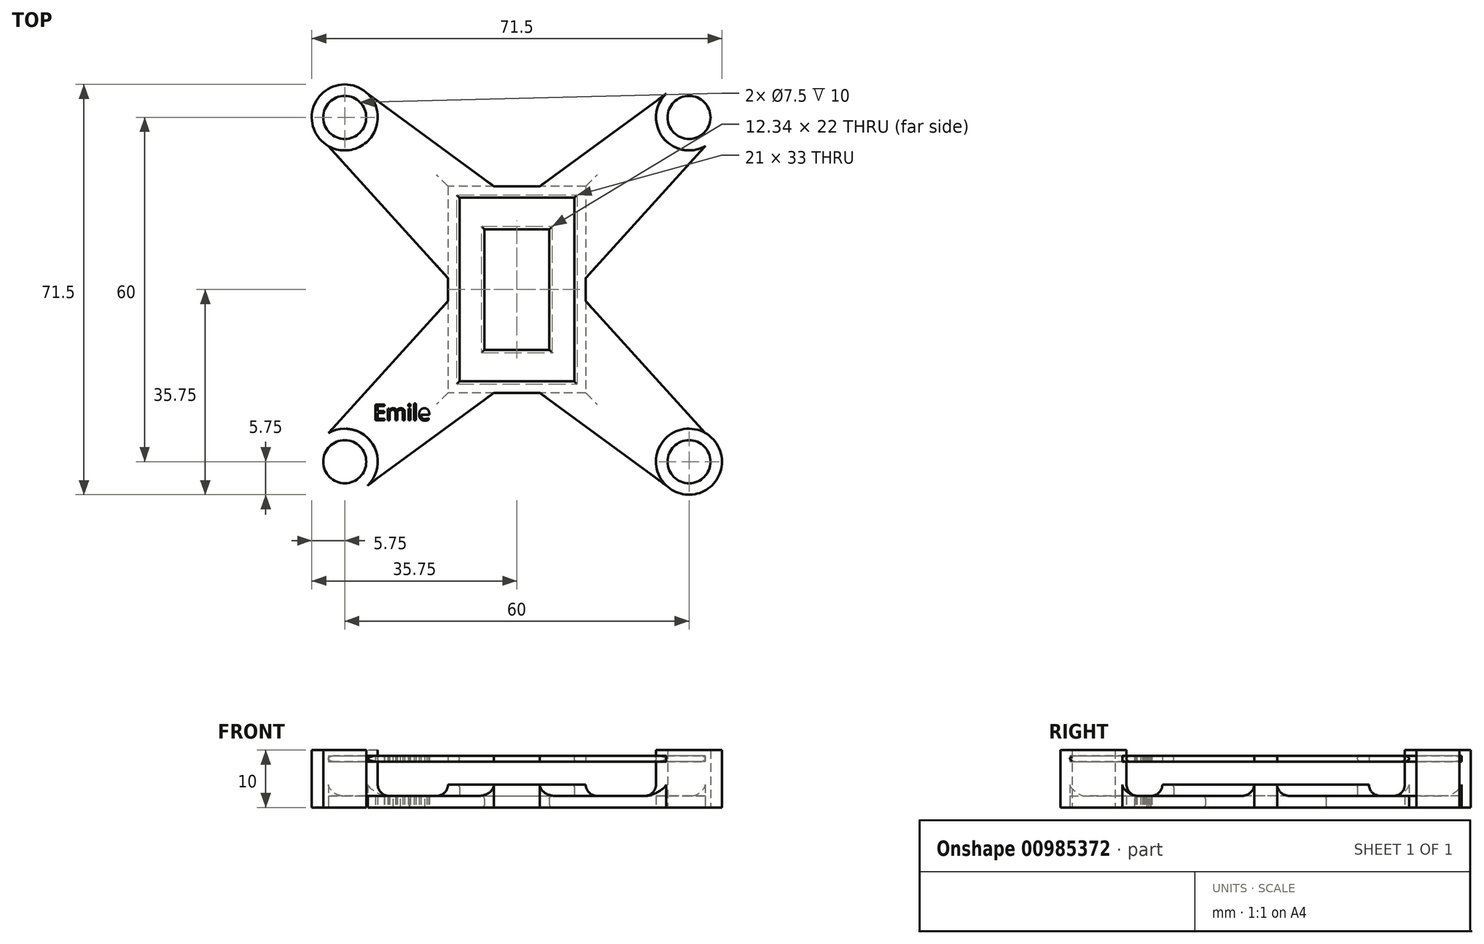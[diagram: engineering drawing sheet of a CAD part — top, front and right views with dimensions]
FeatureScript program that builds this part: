
annotation { "Feature Type Name" : "Feature", "Feature Type Description" : "" }
export const myFeature = defineFeature(function(context is Context, id is Id, definition is map)
    precondition{}
    {
        {
            var Q0;
            Q0=qCreatedBy(makeId("Top.planeOp"),FACE);
            var sketch = newSketch(context, id + "F0", { "sketchPlane" : qUnion([Q0])});
            skLineSegment(sketch, "E0.bottom", {"start": v(30, -30) * mm, "end": v(-30, -30) * mm, "construction": true});
            skLineSegment(sketch, "E0.top", {"start": v(30, 30) * mm, "end": v(-30, 30) * mm, "construction": true});
            skLineSegment(sketch, "E0.left", {"start": v(30, -30) * mm, "end": v(30, 30) * mm, "construction": true});
            skLineSegment(sketch, "E0.right", {"start": v(-30, -30) * mm, "end": v(-30, 30) * mm, "construction": true});
            skPoint(sketch, "E0.middle", {"position": v(0, 0) * mm});
            skCircle(sketch, "E1", {"center": v(-30, 30) * mm, "radius": 3.75 * mm});
            skCircle(sketch, "E2.MirrorC", {"center": v(30, 30) * mm, "radius": 3.75 * mm});
            skCircle(sketch, "E3.MirrorC", {"center": v(-30, -30) * mm, "radius": 3.75 * mm});
            skCircle(sketch, "E4.MirrorC", {"center": v(30, -30) * mm, "radius": 3.75 * mm});
            skCircle(sketch, "E5", {"center": v(-30, 30) * mm, "radius": 5.75 * mm});
            skCircle(sketch, "E6.MirrorC", {"center": v(30, 30) * mm, "radius": 5.75 * mm});
            skCircle(sketch, "E7.MirrorC", {"center": v(30, -30) * mm, "radius": 5.75 * mm});
            skCircle(sketch, "E8.MirrorC", {"center": v(-30, -30) * mm, "radius": 5.75 * mm});
            skLineSegment(sketch, "E9.bottom", {"start": v(10, -16) * mm, "end": v(-10, -16) * mm});
            skLineSegment(sketch, "E9.top", {"start": v(10, 16) * mm, "end": v(-10, 16) * mm});
            skLineSegment(sketch, "E9.left", {"start": v(10, -16) * mm, "end": v(10, 16) * mm});
            skLineSegment(sketch, "E9.right", {"start": v(-10, -16) * mm, "end": v(-10, 16) * mm});
            skLineSegment(sketch, "E10.bottom", {"start": v(12, 18) * mm, "end": v(-12, 18) * mm});
            skLineSegment(sketch, "E10.top", {"start": v(12, -18) * mm, "end": v(-12, -18) * mm});
            skLineSegment(sketch, "E10.left", {"start": v(12, 18) * mm, "end": v(12, -18) * mm});
            skLineSegment(sketch, "E10.right", {"start": v(-12, 18) * mm, "end": v(-12, -18) * mm});
            skLineSegment(sketch, "E11", {"start": v(-26, 34.13) * mm, "end": v(-4, 18) * mm});
            skLineSegment(sketch, "E12", {"start": v(-32.84, 25) * mm, "end": v(-12, 2) * mm});
            skLineSegment(sketch, "E13.MirrorCS", {"start": v(26, 34.13) * mm, "end": v(4, 18) * mm});
            skLineSegment(sketch, "E14.MirrorCS", {"start": v(32.84, 25) * mm, "end": v(12, 2) * mm});
            skLineSegment(sketch, "E15.MirrorCS", {"start": v(-32.84, -25) * mm, "end": v(-12, -2) * mm});
            skLineSegment(sketch, "E16.MirrorCS", {"start": v(-26, -34.13) * mm, "end": v(-4, -18) * mm});
            skLineSegment(sketch, "E17.MirrorCS", {"start": v(26, -34.13) * mm, "end": v(4, -18) * mm});
            skLineSegment(sketch, "E18.MirrorCS", {"start": v(32.84, -25) * mm, "end": v(12, -2) * mm});
            skLineSegment(sketch, "E19.bottom", {"start": v(-5.67, 10.5) * mm, "end": v(5.67, 10.5) * mm});
            skLineSegment(sketch, "E19.top", {"start": v(-5.67, -10.5) * mm, "end": v(5.67, -10.5) * mm});
            skLineSegment(sketch, "E19.left", {"start": v(-5.67, 10.5) * mm, "end": v(-5.67, -10.5) * mm});
            skLineSegment(sketch, "E19.right", {"start": v(5.67, 10.5) * mm, "end": v(5.67, -10.5) * mm});
            skText(sketch, "E20", { "text": "Emile\n", "fontName": "OpenSans-Regular.ttf"});
            const initialGuessF0  = {"E20": [-0.025, -0.0228, 1, 0, 0.0028]};
            skSetInitialGuess(sketch, initialGuessF0);
            skSolve(sketch);
        }
        {
            var Q0;
            Q0=makeQuery(id+"F0.imprint","IMPRINT",FACE,{"disambiguationData":[TD([[makeQuery(id+"F0.imprint","IMPRINT",EDGE,{"derivedFrom":sQuery(id+"F0.wireOp",EDGE,"E9.bottom")}),1.0]])]});
            var Q1;
            Q1=makeQuery(id+"F0.imprint","IMPRINT",FACE,{"disambiguationData":[TD([[makeQuery(id+"F0.imprint","IMPRINT",EDGE,{"derivedFrom":sQuery(id+"F0.wireOp",EDGE,"E9.bottom")}),-1.0]])]});
            var Q2;
            {var subQ0=sQuery(id+"F0.wireOp",EDGE,"E11");Q2=makeQuery(id+"F0.imprint","IMPRINT",FACE,{"disambiguationData":[TD([[makeQuery(id+"F0.imprint","IMPRINT",EDGE,{"derivedFrom":subQ0}),-1.0]])]});}
            var Q3;
            {var subQ0=sQuery(id+"F0.wireOp",EDGE,"E15.MirrorCS");Q3=makeQuery(id+"F0.imprint","IMPRINT",FACE,{"disambiguationData":[TD([[makeQuery(id+"F0.imprint","IMPRINT",EDGE,{"derivedFrom":subQ0}),-1.0]])]});}
            var Q4;
            {var subQ0=sQuery(id+"F0.wireOp",EDGE,"E17.MirrorCS");Q4=makeQuery(id+"F0.imprint","IMPRINT",FACE,{"disambiguationData":[TD([[makeQuery(id+"F0.imprint","IMPRINT",EDGE,{"derivedFrom":subQ0}),-1.0]])]});}
            var Q5;
            {var subQ0=sQuery(id+"F0.wireOp",EDGE,"E13.MirrorCS");Q5=makeQuery(id+"F0.imprint","IMPRINT",FACE,{"disambiguationData":[TD([[makeQuery(id+"F0.imprint","IMPRINT",EDGE,{"derivedFrom":subQ0}),1.0]])]});}
            var Q6;
            Q6=makeQuery(id+"F0.imprint","IMPRINT",FACE,{"disambiguationData":[TD([[makeQuery(id+"F0.imprint","IMPRINT",EDGE,{"derivedFrom":sQuery(id+"F0.wireOp",EDGE,"E1")}),-1.0]])]});
            var Q7;
            Q7=makeQuery(id+"F0.imprint","IMPRINT",FACE,{"disambiguationData":[TD([[makeQuery(id+"F0.imprint","IMPRINT",EDGE,{"derivedFrom":sQuery(id+"F0.wireOp",EDGE,"E2.MirrorC")}),1.0]])]});
            var Q8;
            Q8=makeQuery(id+"F0.imprint","IMPRINT",FACE,{"disambiguationData":[TD([[makeQuery(id+"F0.imprint","IMPRINT",EDGE,{"derivedFrom":sQuery(id+"F0.wireOp",EDGE,"E4.MirrorC")}),-1.0]])]});
            var Q9;
            Q9=makeQuery(id+"F0.imprint","IMPRINT",FACE,{"disambiguationData":[TD([[makeQuery(id+"F0.imprint","IMPRINT",EDGE,{"derivedFrom":sQuery(id+"F0.wireOp",EDGE,"E3.MirrorC")}),1.0]])]});
            extrude(context, id + "F1", {"entities" : qUnion([Q0, Q1, Q2, Q3, Q4, Q5, Q6, Q7, Q8, Q9]), "depth" : 2 * mm, "offsetDistance" : 25 * mm});
        }
        {
            var Q0;
            Q0=makeQuery(id+"F0.imprint","IMPRINT",FACE,{"disambiguationData":[TD([[makeQuery(id+"F0.imprint","IMPRINT",EDGE,{"derivedFrom":sQuery(id+"F0.wireOp",EDGE,"E1")}),-1.0]])]});
            var Q1;
            Q1=makeQuery(id+"F0.imprint","IMPRINT",FACE,{"disambiguationData":[TD([[makeQuery(id+"F0.imprint","IMPRINT",EDGE,{"derivedFrom":sQuery(id+"F0.wireOp",EDGE,"E2.MirrorC")}),1.0]])]});
            var Q2;
            Q2=makeQuery(id+"F0.imprint","IMPRINT",FACE,{"disambiguationData":[TD([[makeQuery(id+"F0.imprint","IMPRINT",EDGE,{"derivedFrom":sQuery(id+"F0.wireOp",EDGE,"E4.MirrorC")}),-1.0]])]});
            var Q3;
            Q3=makeQuery(id+"F0.imprint","IMPRINT",FACE,{"disambiguationData":[TD([[makeQuery(id+"F0.imprint","IMPRINT",EDGE,{"derivedFrom":sQuery(id+"F0.wireOp",EDGE,"E3.MirrorC")}),1.0]])]});
            extrude(context, id + "F2", {"entities" : qUnion([Q0, Q1, Q2, Q3]), "operationType" : NewBodyOperationType.ADD, "depth" : 10 * mm, "offsetDistance" : 25 * mm});
        }
        {
            var Q0;
            Q0=makeQuery(id+"F0.imprint","IMPRINT",FACE,{"disambiguationData":[TD([[makeQuery(id+"F0.imprint","IMPRINT",EDGE,{"derivedFrom":sQuery(id+"F0.wireOp",EDGE,"E9.bottom")}),1.0]])]});
            extrude(context, id + "F3", {"entities" : qUnion([Q0]), "operationType" : NewBodyOperationType.ADD, "depth" : 4 * mm, "offsetDistance" : 25 * mm});
        }
        {
            var Q0;
            {var subQ0=sQuery(id+"F0.wireOp",EDGE,"E5");Q0=makeQuery(id+"F2.boolean.opBoolean","INTERSECT",EDGE,{"derivedFrom":[makeQuery(id+"F1.opExtrude","CAP_FACE",FACE,{"disambiguationData":[OSD([sQuery(id+"F0.wireOp",EDGE,"E1"),sQuery(id+"F0.wireOp",EDGE,"E2.MirrorC"),sQuery(id+"F0.wireOp",EDGE,"E3.MirrorC"),sQuery(id+"F0.wireOp",EDGE,"E4.MirrorC"),subQ0,sQuery(id+"F0.wireOp",EDGE,"E6.MirrorC"),sQuery(id+"F0.wireOp",EDGE,"E7.MirrorC"),sQuery(id+"F0.wireOp",EDGE,"E8.MirrorC"),sQuery(id+"F0.wireOp",EDGE,"E10.bottom"),sQuery(id+"F0.wireOp",EDGE,"E10.top"),sQuery(id+"F0.wireOp",EDGE,"E10.left"),sQuery(id+"F0.wireOp",EDGE,"E10.right"),sQuery(id+"F0.wireOp",EDGE,"E11"),sQuery(id+"F0.wireOp",EDGE,"E12"),sQuery(id+"F0.wireOp",EDGE,"E13.MirrorCS"),sQuery(id+"F0.wireOp",EDGE,"E14.MirrorCS"),sQuery(id+"F0.wireOp",EDGE,"E15.MirrorCS"),sQuery(id+"F0.wireOp",EDGE,"E16.MirrorCS"),sQuery(id+"F0.wireOp",EDGE,"E17.MirrorCS"),sQuery(id+"F0.wireOp",EDGE,"E18.MirrorCS"),sQuery(id+"F0.wireOp",EDGE,"E19.bottom"),sQuery(id+"F0.wireOp",EDGE,"E19.top"),sQuery(id+"F0.wireOp",EDGE,"E19.left"),sQuery(id+"F0.wireOp",EDGE,"E19.right")])],"isStart":false}),makeQuery(id+"F2.opExtrude","SWEPT_FACE",FACE,{"disambiguationData":[OSD([subQ0])]})]});}
            var Q1;
            {var subQ0=sQuery(id+"F0.wireOp",EDGE,"E6.MirrorC");Q1=makeQuery(id+"F2.boolean.opBoolean","INTERSECT",EDGE,{"derivedFrom":[makeQuery(id+"F1.opExtrude","CAP_FACE",FACE,{"disambiguationData":[OSD([sQuery(id+"F0.wireOp",EDGE,"E1"),sQuery(id+"F0.wireOp",EDGE,"E2.MirrorC"),sQuery(id+"F0.wireOp",EDGE,"E3.MirrorC"),sQuery(id+"F0.wireOp",EDGE,"E4.MirrorC"),sQuery(id+"F0.wireOp",EDGE,"E5"),subQ0,sQuery(id+"F0.wireOp",EDGE,"E7.MirrorC"),sQuery(id+"F0.wireOp",EDGE,"E8.MirrorC"),sQuery(id+"F0.wireOp",EDGE,"E10.bottom"),sQuery(id+"F0.wireOp",EDGE,"E10.top"),sQuery(id+"F0.wireOp",EDGE,"E10.left"),sQuery(id+"F0.wireOp",EDGE,"E10.right"),sQuery(id+"F0.wireOp",EDGE,"E11"),sQuery(id+"F0.wireOp",EDGE,"E12"),sQuery(id+"F0.wireOp",EDGE,"E13.MirrorCS"),sQuery(id+"F0.wireOp",EDGE,"E14.MirrorCS"),sQuery(id+"F0.wireOp",EDGE,"E15.MirrorCS"),sQuery(id+"F0.wireOp",EDGE,"E16.MirrorCS"),sQuery(id+"F0.wireOp",EDGE,"E17.MirrorCS"),sQuery(id+"F0.wireOp",EDGE,"E18.MirrorCS"),sQuery(id+"F0.wireOp",EDGE,"E19.bottom"),sQuery(id+"F0.wireOp",EDGE,"E19.top"),sQuery(id+"F0.wireOp",EDGE,"E19.left"),sQuery(id+"F0.wireOp",EDGE,"E19.right")])],"isStart":false}),makeQuery(id+"F2.opExtrude","SWEPT_FACE",FACE,{"disambiguationData":[OSD([subQ0])]})]});}
            var Q2;
            {var subQ0=sQuery(id+"F0.wireOp",EDGE,"E7.MirrorC");Q2=makeQuery(id+"F2.boolean.opBoolean","INTERSECT",EDGE,{"derivedFrom":[makeQuery(id+"F1.opExtrude","CAP_FACE",FACE,{"disambiguationData":[OSD([sQuery(id+"F0.wireOp",EDGE,"E1"),sQuery(id+"F0.wireOp",EDGE,"E2.MirrorC"),sQuery(id+"F0.wireOp",EDGE,"E3.MirrorC"),sQuery(id+"F0.wireOp",EDGE,"E4.MirrorC"),sQuery(id+"F0.wireOp",EDGE,"E5"),sQuery(id+"F0.wireOp",EDGE,"E6.MirrorC"),subQ0,sQuery(id+"F0.wireOp",EDGE,"E8.MirrorC"),sQuery(id+"F0.wireOp",EDGE,"E10.bottom"),sQuery(id+"F0.wireOp",EDGE,"E10.top"),sQuery(id+"F0.wireOp",EDGE,"E10.left"),sQuery(id+"F0.wireOp",EDGE,"E10.right"),sQuery(id+"F0.wireOp",EDGE,"E11"),sQuery(id+"F0.wireOp",EDGE,"E12"),sQuery(id+"F0.wireOp",EDGE,"E13.MirrorCS"),sQuery(id+"F0.wireOp",EDGE,"E14.MirrorCS"),sQuery(id+"F0.wireOp",EDGE,"E15.MirrorCS"),sQuery(id+"F0.wireOp",EDGE,"E16.MirrorCS"),sQuery(id+"F0.wireOp",EDGE,"E17.MirrorCS"),sQuery(id+"F0.wireOp",EDGE,"E18.MirrorCS"),sQuery(id+"F0.wireOp",EDGE,"E19.bottom"),sQuery(id+"F0.wireOp",EDGE,"E19.top"),sQuery(id+"F0.wireOp",EDGE,"E19.left"),sQuery(id+"F0.wireOp",EDGE,"E19.right")])],"isStart":false}),makeQuery(id+"F2.opExtrude","SWEPT_FACE",FACE,{"disambiguationData":[OSD([subQ0])]})]});}
            var Q3;
            {var subQ0=sQuery(id+"F0.wireOp",EDGE,"E8.MirrorC");Q3=makeQuery(id+"F2.boolean.opBoolean","INTERSECT",EDGE,{"derivedFrom":[makeQuery(id+"F1.opExtrude","CAP_FACE",FACE,{"disambiguationData":[OSD([sQuery(id+"F0.wireOp",EDGE,"E1"),sQuery(id+"F0.wireOp",EDGE,"E2.MirrorC"),sQuery(id+"F0.wireOp",EDGE,"E3.MirrorC"),sQuery(id+"F0.wireOp",EDGE,"E4.MirrorC"),sQuery(id+"F0.wireOp",EDGE,"E5"),sQuery(id+"F0.wireOp",EDGE,"E6.MirrorC"),sQuery(id+"F0.wireOp",EDGE,"E7.MirrorC"),subQ0,sQuery(id+"F0.wireOp",EDGE,"E10.bottom"),sQuery(id+"F0.wireOp",EDGE,"E10.top"),sQuery(id+"F0.wireOp",EDGE,"E10.left"),sQuery(id+"F0.wireOp",EDGE,"E10.right"),sQuery(id+"F0.wireOp",EDGE,"E11"),sQuery(id+"F0.wireOp",EDGE,"E12"),sQuery(id+"F0.wireOp",EDGE,"E13.MirrorCS"),sQuery(id+"F0.wireOp",EDGE,"E14.MirrorCS"),sQuery(id+"F0.wireOp",EDGE,"E15.MirrorCS"),sQuery(id+"F0.wireOp",EDGE,"E16.MirrorCS"),sQuery(id+"F0.wireOp",EDGE,"E17.MirrorCS"),sQuery(id+"F0.wireOp",EDGE,"E18.MirrorCS"),sQuery(id+"F0.wireOp",EDGE,"E19.bottom"),sQuery(id+"F0.wireOp",EDGE,"E19.top"),sQuery(id+"F0.wireOp",EDGE,"E19.left"),sQuery(id+"F0.wireOp",EDGE,"E19.right")])],"isStart":false}),makeQuery(id+"F2.opExtrude","SWEPT_FACE",FACE,{"disambiguationData":[OSD([subQ0])]})]});}
            var Q4;
            {var subQ0=sQuery(id+"F0.wireOp",EDGE,"E10.right");Q4=makeQuery(id+"F3.boolean.opBoolean","INTERSECT",EDGE,{"disambiguationData":[OD(1.0)],"derivedFrom":[makeQuery(id+"F1.opExtrude","CAP_FACE",FACE,{"disambiguationData":[OSD([sQuery(id+"F0.wireOp",EDGE,"E1"),sQuery(id+"F0.wireOp",EDGE,"E2.MirrorC"),sQuery(id+"F0.wireOp",EDGE,"E3.MirrorC"),sQuery(id+"F0.wireOp",EDGE,"E4.MirrorC"),sQuery(id+"F0.wireOp",EDGE,"E5"),sQuery(id+"F0.wireOp",EDGE,"E6.MirrorC"),sQuery(id+"F0.wireOp",EDGE,"E7.MirrorC"),sQuery(id+"F0.wireOp",EDGE,"E8.MirrorC"),sQuery(id+"F0.wireOp",EDGE,"E10.bottom"),sQuery(id+"F0.wireOp",EDGE,"E10.top"),sQuery(id+"F0.wireOp",EDGE,"E10.left"),subQ0,sQuery(id+"F0.wireOp",EDGE,"E11"),sQuery(id+"F0.wireOp",EDGE,"E12"),sQuery(id+"F0.wireOp",EDGE,"E13.MirrorCS"),sQuery(id+"F0.wireOp",EDGE,"E14.MirrorCS"),sQuery(id+"F0.wireOp",EDGE,"E15.MirrorCS"),sQuery(id+"F0.wireOp",EDGE,"E16.MirrorCS"),sQuery(id+"F0.wireOp",EDGE,"E17.MirrorCS"),sQuery(id+"F0.wireOp",EDGE,"E18.MirrorCS"),sQuery(id+"F0.wireOp",EDGE,"E19.bottom"),sQuery(id+"F0.wireOp",EDGE,"E19.top"),sQuery(id+"F0.wireOp",EDGE,"E19.left"),sQuery(id+"F0.wireOp",EDGE,"E19.right")])],"isStart":false}),makeQuery(id+"F3.opExtrude","SWEPT_FACE",FACE,{"disambiguationData":[OSD([subQ0])]})]});}
            var Q5;
            {var subQ0=sQuery(id+"F0.wireOp",EDGE,"E10.top");Q5=makeQuery(id+"F3.boolean.opBoolean","INTERSECT",EDGE,{"disambiguationData":[OD(0.0)],"derivedFrom":[makeQuery(id+"F1.opExtrude","CAP_FACE",FACE,{"disambiguationData":[OSD([sQuery(id+"F0.wireOp",EDGE,"E1"),sQuery(id+"F0.wireOp",EDGE,"E2.MirrorC"),sQuery(id+"F0.wireOp",EDGE,"E3.MirrorC"),sQuery(id+"F0.wireOp",EDGE,"E4.MirrorC"),sQuery(id+"F0.wireOp",EDGE,"E5"),sQuery(id+"F0.wireOp",EDGE,"E6.MirrorC"),sQuery(id+"F0.wireOp",EDGE,"E7.MirrorC"),sQuery(id+"F0.wireOp",EDGE,"E8.MirrorC"),sQuery(id+"F0.wireOp",EDGE,"E10.bottom"),subQ0,sQuery(id+"F0.wireOp",EDGE,"E10.left"),sQuery(id+"F0.wireOp",EDGE,"E10.right"),sQuery(id+"F0.wireOp",EDGE,"E11"),sQuery(id+"F0.wireOp",EDGE,"E12"),sQuery(id+"F0.wireOp",EDGE,"E13.MirrorCS"),sQuery(id+"F0.wireOp",EDGE,"E14.MirrorCS"),sQuery(id+"F0.wireOp",EDGE,"E15.MirrorCS"),sQuery(id+"F0.wireOp",EDGE,"E16.MirrorCS"),sQuery(id+"F0.wireOp",EDGE,"E17.MirrorCS"),sQuery(id+"F0.wireOp",EDGE,"E18.MirrorCS"),sQuery(id+"F0.wireOp",EDGE,"E19.bottom"),sQuery(id+"F0.wireOp",EDGE,"E19.top"),sQuery(id+"F0.wireOp",EDGE,"E19.left"),sQuery(id+"F0.wireOp",EDGE,"E19.right")])],"isStart":false}),makeQuery(id+"F3.opExtrude","SWEPT_FACE",FACE,{"disambiguationData":[OSD([subQ0])]})]});}
            var Q6;
            {var subQ0=sQuery(id+"F0.wireOp",EDGE,"E10.top");Q6=makeQuery(id+"F3.boolean.opBoolean","INTERSECT",EDGE,{"disambiguationData":[OD(1.0)],"derivedFrom":[makeQuery(id+"F1.opExtrude","CAP_FACE",FACE,{"disambiguationData":[OSD([sQuery(id+"F0.wireOp",EDGE,"E1"),sQuery(id+"F0.wireOp",EDGE,"E2.MirrorC"),sQuery(id+"F0.wireOp",EDGE,"E3.MirrorC"),sQuery(id+"F0.wireOp",EDGE,"E4.MirrorC"),sQuery(id+"F0.wireOp",EDGE,"E5"),sQuery(id+"F0.wireOp",EDGE,"E6.MirrorC"),sQuery(id+"F0.wireOp",EDGE,"E7.MirrorC"),sQuery(id+"F0.wireOp",EDGE,"E8.MirrorC"),sQuery(id+"F0.wireOp",EDGE,"E10.bottom"),subQ0,sQuery(id+"F0.wireOp",EDGE,"E10.left"),sQuery(id+"F0.wireOp",EDGE,"E10.right"),sQuery(id+"F0.wireOp",EDGE,"E11"),sQuery(id+"F0.wireOp",EDGE,"E12"),sQuery(id+"F0.wireOp",EDGE,"E13.MirrorCS"),sQuery(id+"F0.wireOp",EDGE,"E14.MirrorCS"),sQuery(id+"F0.wireOp",EDGE,"E15.MirrorCS"),sQuery(id+"F0.wireOp",EDGE,"E16.MirrorCS"),sQuery(id+"F0.wireOp",EDGE,"E17.MirrorCS"),sQuery(id+"F0.wireOp",EDGE,"E18.MirrorCS"),sQuery(id+"F0.wireOp",EDGE,"E19.bottom"),sQuery(id+"F0.wireOp",EDGE,"E19.top"),sQuery(id+"F0.wireOp",EDGE,"E19.left"),sQuery(id+"F0.wireOp",EDGE,"E19.right")])],"isStart":false}),makeQuery(id+"F3.opExtrude","SWEPT_FACE",FACE,{"disambiguationData":[OSD([subQ0])]})]});}
            var Q7;
            {var subQ0=sQuery(id+"F0.wireOp",EDGE,"E10.left");Q7=makeQuery(id+"F3.boolean.opBoolean","INTERSECT",EDGE,{"disambiguationData":[OD(1.0)],"derivedFrom":[makeQuery(id+"F1.opExtrude","CAP_FACE",FACE,{"disambiguationData":[OSD([sQuery(id+"F0.wireOp",EDGE,"E1"),sQuery(id+"F0.wireOp",EDGE,"E2.MirrorC"),sQuery(id+"F0.wireOp",EDGE,"E3.MirrorC"),sQuery(id+"F0.wireOp",EDGE,"E4.MirrorC"),sQuery(id+"F0.wireOp",EDGE,"E5"),sQuery(id+"F0.wireOp",EDGE,"E6.MirrorC"),sQuery(id+"F0.wireOp",EDGE,"E7.MirrorC"),sQuery(id+"F0.wireOp",EDGE,"E8.MirrorC"),sQuery(id+"F0.wireOp",EDGE,"E10.bottom"),sQuery(id+"F0.wireOp",EDGE,"E10.top"),subQ0,sQuery(id+"F0.wireOp",EDGE,"E10.right"),sQuery(id+"F0.wireOp",EDGE,"E11"),sQuery(id+"F0.wireOp",EDGE,"E12"),sQuery(id+"F0.wireOp",EDGE,"E13.MirrorCS"),sQuery(id+"F0.wireOp",EDGE,"E14.MirrorCS"),sQuery(id+"F0.wireOp",EDGE,"E15.MirrorCS"),sQuery(id+"F0.wireOp",EDGE,"E16.MirrorCS"),sQuery(id+"F0.wireOp",EDGE,"E17.MirrorCS"),sQuery(id+"F0.wireOp",EDGE,"E18.MirrorCS"),sQuery(id+"F0.wireOp",EDGE,"E19.bottom"),sQuery(id+"F0.wireOp",EDGE,"E19.top"),sQuery(id+"F0.wireOp",EDGE,"E19.left"),sQuery(id+"F0.wireOp",EDGE,"E19.right")])],"isStart":false}),makeQuery(id+"F3.opExtrude","SWEPT_FACE",FACE,{"disambiguationData":[OSD([subQ0])]})]});}
            var Q8;
            {var subQ0=sQuery(id+"F0.wireOp",EDGE,"E10.left");Q8=makeQuery(id+"F3.boolean.opBoolean","INTERSECT",EDGE,{"disambiguationData":[OD(0.0)],"derivedFrom":[makeQuery(id+"F1.opExtrude","CAP_FACE",FACE,{"disambiguationData":[OSD([sQuery(id+"F0.wireOp",EDGE,"E1"),sQuery(id+"F0.wireOp",EDGE,"E2.MirrorC"),sQuery(id+"F0.wireOp",EDGE,"E3.MirrorC"),sQuery(id+"F0.wireOp",EDGE,"E4.MirrorC"),sQuery(id+"F0.wireOp",EDGE,"E5"),sQuery(id+"F0.wireOp",EDGE,"E6.MirrorC"),sQuery(id+"F0.wireOp",EDGE,"E7.MirrorC"),sQuery(id+"F0.wireOp",EDGE,"E8.MirrorC"),sQuery(id+"F0.wireOp",EDGE,"E10.bottom"),sQuery(id+"F0.wireOp",EDGE,"E10.top"),subQ0,sQuery(id+"F0.wireOp",EDGE,"E10.right"),sQuery(id+"F0.wireOp",EDGE,"E11"),sQuery(id+"F0.wireOp",EDGE,"E12"),sQuery(id+"F0.wireOp",EDGE,"E13.MirrorCS"),sQuery(id+"F0.wireOp",EDGE,"E14.MirrorCS"),sQuery(id+"F0.wireOp",EDGE,"E15.MirrorCS"),sQuery(id+"F0.wireOp",EDGE,"E16.MirrorCS"),sQuery(id+"F0.wireOp",EDGE,"E17.MirrorCS"),sQuery(id+"F0.wireOp",EDGE,"E18.MirrorCS"),sQuery(id+"F0.wireOp",EDGE,"E19.bottom"),sQuery(id+"F0.wireOp",EDGE,"E19.top"),sQuery(id+"F0.wireOp",EDGE,"E19.left"),sQuery(id+"F0.wireOp",EDGE,"E19.right")])],"isStart":false}),makeQuery(id+"F3.opExtrude","SWEPT_FACE",FACE,{"disambiguationData":[OSD([subQ0])]})]});}
            var Q9;
            {var subQ0=sQuery(id+"F0.wireOp",EDGE,"E10.bottom");Q9=makeQuery(id+"F3.boolean.opBoolean","INTERSECT",EDGE,{"disambiguationData":[OD(1.0)],"derivedFrom":[makeQuery(id+"F1.opExtrude","CAP_FACE",FACE,{"disambiguationData":[OSD([sQuery(id+"F0.wireOp",EDGE,"E1"),sQuery(id+"F0.wireOp",EDGE,"E2.MirrorC"),sQuery(id+"F0.wireOp",EDGE,"E3.MirrorC"),sQuery(id+"F0.wireOp",EDGE,"E4.MirrorC"),sQuery(id+"F0.wireOp",EDGE,"E5"),sQuery(id+"F0.wireOp",EDGE,"E6.MirrorC"),sQuery(id+"F0.wireOp",EDGE,"E7.MirrorC"),sQuery(id+"F0.wireOp",EDGE,"E8.MirrorC"),subQ0,sQuery(id+"F0.wireOp",EDGE,"E10.top"),sQuery(id+"F0.wireOp",EDGE,"E10.left"),sQuery(id+"F0.wireOp",EDGE,"E10.right"),sQuery(id+"F0.wireOp",EDGE,"E11"),sQuery(id+"F0.wireOp",EDGE,"E12"),sQuery(id+"F0.wireOp",EDGE,"E13.MirrorCS"),sQuery(id+"F0.wireOp",EDGE,"E14.MirrorCS"),sQuery(id+"F0.wireOp",EDGE,"E15.MirrorCS"),sQuery(id+"F0.wireOp",EDGE,"E16.MirrorCS"),sQuery(id+"F0.wireOp",EDGE,"E17.MirrorCS"),sQuery(id+"F0.wireOp",EDGE,"E18.MirrorCS"),sQuery(id+"F0.wireOp",EDGE,"E19.bottom"),sQuery(id+"F0.wireOp",EDGE,"E19.top"),sQuery(id+"F0.wireOp",EDGE,"E19.left"),sQuery(id+"F0.wireOp",EDGE,"E19.right")])],"isStart":false}),makeQuery(id+"F3.opExtrude","SWEPT_FACE",FACE,{"disambiguationData":[OSD([subQ0])]})]});}
            var Q10;
            {var subQ0=sQuery(id+"F0.wireOp",EDGE,"E10.bottom");Q10=makeQuery(id+"F3.boolean.opBoolean","INTERSECT",EDGE,{"disambiguationData":[OD(0.0)],"derivedFrom":[makeQuery(id+"F1.opExtrude","CAP_FACE",FACE,{"disambiguationData":[OSD([sQuery(id+"F0.wireOp",EDGE,"E1"),sQuery(id+"F0.wireOp",EDGE,"E2.MirrorC"),sQuery(id+"F0.wireOp",EDGE,"E3.MirrorC"),sQuery(id+"F0.wireOp",EDGE,"E4.MirrorC"),sQuery(id+"F0.wireOp",EDGE,"E5"),sQuery(id+"F0.wireOp",EDGE,"E6.MirrorC"),sQuery(id+"F0.wireOp",EDGE,"E7.MirrorC"),sQuery(id+"F0.wireOp",EDGE,"E8.MirrorC"),subQ0,sQuery(id+"F0.wireOp",EDGE,"E10.top"),sQuery(id+"F0.wireOp",EDGE,"E10.left"),sQuery(id+"F0.wireOp",EDGE,"E10.right"),sQuery(id+"F0.wireOp",EDGE,"E11"),sQuery(id+"F0.wireOp",EDGE,"E12"),sQuery(id+"F0.wireOp",EDGE,"E13.MirrorCS"),sQuery(id+"F0.wireOp",EDGE,"E14.MirrorCS"),sQuery(id+"F0.wireOp",EDGE,"E15.MirrorCS"),sQuery(id+"F0.wireOp",EDGE,"E16.MirrorCS"),sQuery(id+"F0.wireOp",EDGE,"E17.MirrorCS"),sQuery(id+"F0.wireOp",EDGE,"E18.MirrorCS"),sQuery(id+"F0.wireOp",EDGE,"E19.bottom"),sQuery(id+"F0.wireOp",EDGE,"E19.top"),sQuery(id+"F0.wireOp",EDGE,"E19.left"),sQuery(id+"F0.wireOp",EDGE,"E19.right")])],"isStart":false}),makeQuery(id+"F3.opExtrude","SWEPT_FACE",FACE,{"disambiguationData":[OSD([subQ0])]})]});}
            var Q11;
            {var subQ0=sQuery(id+"F0.wireOp",EDGE,"E10.right");Q11=makeQuery(id+"F3.boolean.opBoolean","INTERSECT",EDGE,{"disambiguationData":[OD(0.0)],"derivedFrom":[makeQuery(id+"F1.opExtrude","CAP_FACE",FACE,{"disambiguationData":[OSD([sQuery(id+"F0.wireOp",EDGE,"E1"),sQuery(id+"F0.wireOp",EDGE,"E2.MirrorC"),sQuery(id+"F0.wireOp",EDGE,"E3.MirrorC"),sQuery(id+"F0.wireOp",EDGE,"E4.MirrorC"),sQuery(id+"F0.wireOp",EDGE,"E5"),sQuery(id+"F0.wireOp",EDGE,"E6.MirrorC"),sQuery(id+"F0.wireOp",EDGE,"E7.MirrorC"),sQuery(id+"F0.wireOp",EDGE,"E8.MirrorC"),sQuery(id+"F0.wireOp",EDGE,"E10.bottom"),sQuery(id+"F0.wireOp",EDGE,"E10.top"),sQuery(id+"F0.wireOp",EDGE,"E10.left"),subQ0,sQuery(id+"F0.wireOp",EDGE,"E11"),sQuery(id+"F0.wireOp",EDGE,"E12"),sQuery(id+"F0.wireOp",EDGE,"E13.MirrorCS"),sQuery(id+"F0.wireOp",EDGE,"E14.MirrorCS"),sQuery(id+"F0.wireOp",EDGE,"E15.MirrorCS"),sQuery(id+"F0.wireOp",EDGE,"E16.MirrorCS"),sQuery(id+"F0.wireOp",EDGE,"E17.MirrorCS"),sQuery(id+"F0.wireOp",EDGE,"E18.MirrorCS"),sQuery(id+"F0.wireOp",EDGE,"E19.bottom"),sQuery(id+"F0.wireOp",EDGE,"E19.top"),sQuery(id+"F0.wireOp",EDGE,"E19.left"),sQuery(id+"F0.wireOp",EDGE,"E19.right")])],"isStart":false}),makeQuery(id+"F3.opExtrude","SWEPT_FACE",FACE,{"disambiguationData":[OSD([subQ0])]})]});}
            fillet(context, id + "F4", {"entities" : qUnion([Q0, Q1, Q2, Q3, Q4, Q5, Q6, Q7, Q8, Q9, Q10, Q11]), "radius" : 2 * mm, "tangentPropagation" : true, "allowEdgeOverflow" : false});
        }
        {
            var Q0;
            Q0=makeQuery(id+"F0.imprint","IMPRINT",FACE,{"disambiguationData":[TD([[makeQuery(id+"F0.imprint","IMPRINT",EDGE,{"derivedFrom":sQuery(id+"F0.wireOp",EDGE,"E9.bottom")}),1.0]])]});
            var Q1;
            {var subQ0=sQuery(id+"F0.wireOp",EDGE,"E15.MirrorCS");Q1=makeQuery(id+"F0.imprint","IMPRINT",FACE,{"disambiguationData":[TD([[makeQuery(id+"F0.imprint","IMPRINT",EDGE,{"derivedFrom":subQ0}),-1.0]])]});}
            var Q2;
            {var subQ0=sQuery(id+"F0.wireOp",EDGE,"E11");Q2=makeQuery(id+"F0.imprint","IMPRINT",FACE,{"disambiguationData":[TD([[makeQuery(id+"F0.imprint","IMPRINT",EDGE,{"derivedFrom":subQ0}),-1.0]])]});}
            var Q3;
            {var subQ0=sQuery(id+"F0.wireOp",EDGE,"E13.MirrorCS");Q3=makeQuery(id+"F0.imprint","IMPRINT",FACE,{"disambiguationData":[TD([[makeQuery(id+"F0.imprint","IMPRINT",EDGE,{"derivedFrom":subQ0}),1.0]])]});}
            var Q4;
            {var subQ0=sQuery(id+"F0.wireOp",EDGE,"E17.MirrorCS");Q4=makeQuery(id+"F0.imprint","IMPRINT",FACE,{"disambiguationData":[TD([[makeQuery(id+"F0.imprint","IMPRINT",EDGE,{"derivedFrom":subQ0}),-1.0]])]});}
            extrude(context, id + "F5", {"entities" : qUnion([Q0, Q1, Q2, Q3, Q4]), "operationType" : NewBodyOperationType.ADD, "depth" : 9 * mm, "offsetDistance" : 25 * mm, "hasSecondDirection" : true, "secondDirectionOppositeDirection" : false, "secondDirectionDepth" : 8 * mm});
        }
        {
            var Q0;
            Q0=makeQuery(id+"F5.opExtrude","CAP_EDGE",EDGE,{"disambiguationData":[OSD([sQuery(id+"F0.wireOp",EDGE,"E7.MirrorC")])],"isStart":true});
            var Q1;
            Q1=makeQuery(id+"F5.opExtrude","CAP_EDGE",EDGE,{"disambiguationData":[OSD([sQuery(id+"F0.wireOp",EDGE,"E6.MirrorC")])],"isStart":true});
            var Q2;
            Q2=makeQuery(id+"F5.opExtrude","CAP_EDGE",EDGE,{"disambiguationData":[OSD([sQuery(id+"F0.wireOp",EDGE,"E5")])],"isStart":true});
            var Q3;
            Q3=makeQuery(id+"F5.opExtrude","CAP_EDGE",EDGE,{"disambiguationData":[OSD([sQuery(id+"F0.wireOp",EDGE,"E8.MirrorC")])],"isStart":true});
            var Q4;
            Q4=makeQuery(id+"F5.opExtrude","CAP_EDGE",EDGE,{"disambiguationData":[OSD([sQuery(id+"F0.wireOp",EDGE,"E9.right")])],"isStart":false});
            var Q5;
            Q5=makeQuery(id+"F5.opExtrude","CAP_EDGE",EDGE,{"disambiguationData":[OSD([sQuery(id+"F0.wireOp",EDGE,"E9.right")])],"isStart":true});
            var Q6;
            Q6=makeQuery(id+"F5.opExtrude","CAP_EDGE",EDGE,{"disambiguationData":[OSD([sQuery(id+"F0.wireOp",EDGE,"E9.top")])],"isStart":false});
            var Q7;
            Q7=makeQuery(id+"F5.opExtrude","CAP_EDGE",EDGE,{"disambiguationData":[OSD([sQuery(id+"F0.wireOp",EDGE,"E9.top")])],"isStart":true});
            var Q8;
            Q8=makeQuery(id+"F5.opExtrude","CAP_EDGE",EDGE,{"disambiguationData":[OSD([sQuery(id+"F0.wireOp",EDGE,"E9.bottom")])],"isStart":true});
            var Q9;
            Q9=makeQuery(id+"F5.opExtrude","CAP_EDGE",EDGE,{"disambiguationData":[OSD([sQuery(id+"F0.wireOp",EDGE,"E9.bottom")])],"isStart":false});
            var Q10;
            Q10=makeQuery(id+"F5.opExtrude","CAP_EDGE",EDGE,{"disambiguationData":[OSD([sQuery(id+"F0.wireOp",EDGE,"E9.left")])],"isStart":false});
            var Q11;
            Q11=makeQuery(id+"F5.opExtrude","CAP_EDGE",EDGE,{"disambiguationData":[OSD([sQuery(id+"F0.wireOp",EDGE,"E9.left")])],"isStart":true});
            var Q12;
            Q12=makeQuery(id+"F1.opExtrude","CAP_EDGE",EDGE,{"disambiguationData":[OSD([sQuery(id+"F0.wireOp",EDGE,"E19.top")])],"isStart":false});
            var Q13;
            Q13=makeQuery(id+"F1.opExtrude","CAP_EDGE",EDGE,{"disambiguationData":[OSD([sQuery(id+"F0.wireOp",EDGE,"E19.top")])],"isStart":true});
            var Q14;
            Q14=makeQuery(id+"F1.opExtrude","CAP_EDGE",EDGE,{"disambiguationData":[OSD([sQuery(id+"F0.wireOp",EDGE,"E19.left")])],"isStart":false});
            var Q15;
            Q15=makeQuery(id+"F1.opExtrude","CAP_EDGE",EDGE,{"disambiguationData":[OSD([sQuery(id+"F0.wireOp",EDGE,"E19.left")])],"isStart":true});
            var Q16;
            Q16=makeQuery(id+"F1.opExtrude","CAP_EDGE",EDGE,{"disambiguationData":[OSD([sQuery(id+"F0.wireOp",EDGE,"E19.bottom")])],"isStart":false});
            var Q17;
            Q17=makeQuery(id+"F1.opExtrude","CAP_EDGE",EDGE,{"disambiguationData":[OSD([sQuery(id+"F0.wireOp",EDGE,"E19.bottom")])],"isStart":true});
            var Q18;
            Q18=makeQuery(id+"F1.opExtrude","CAP_EDGE",EDGE,{"disambiguationData":[OSD([sQuery(id+"F0.wireOp",EDGE,"E19.right")])],"isStart":false});
            var Q19;
            Q19=makeQuery(id+"F1.opExtrude","CAP_EDGE",EDGE,{"disambiguationData":[OSD([sQuery(id+"F0.wireOp",EDGE,"E19.right")])],"isStart":true});
            var Q20;
            Q20=makeQuery(id+"F3.opExtrude","CAP_EDGE",EDGE,{"disambiguationData":[OSD([sQuery(id+"F0.wireOp",EDGE,"E9.bottom")])],"isStart":false});
            var Q21;
            Q21=makeQuery(id+"F3.opExtrude","CAP_EDGE",EDGE,{"disambiguationData":[OSD([sQuery(id+"F0.wireOp",EDGE,"E9.right")])],"isStart":false});
            var Q22;
            Q22=makeQuery(id+"F3.opExtrude","CAP_EDGE",EDGE,{"disambiguationData":[OSD([sQuery(id+"F0.wireOp",EDGE,"E9.top")])],"isStart":false});
            var Q23;
            Q23=makeQuery(id+"F3.opExtrude","CAP_EDGE",EDGE,{"disambiguationData":[OSD([sQuery(id+"F0.wireOp",EDGE,"E9.left")])],"isStart":false});
            var Q24;
            Q24=makeQuery(id+"F5.opExtrude","CAP_EDGE",EDGE,{"disambiguationData":[OSD([sQuery(id+"F0.wireOp",EDGE,"E8.MirrorC")])],"isStart":false});
            var Q25;
            Q25=makeQuery(id+"F5.opExtrude","CAP_EDGE",EDGE,{"disambiguationData":[OSD([sQuery(id+"F0.wireOp",EDGE,"E5")])],"isStart":false});
            var Q26;
            Q26=makeQuery(id+"F5.opExtrude","CAP_EDGE",EDGE,{"disambiguationData":[OSD([sQuery(id+"F0.wireOp",EDGE,"E7.MirrorC")])],"isStart":false});
            var Q27;
            Q27=makeQuery(id+"F5.opExtrude","CAP_EDGE",EDGE,{"disambiguationData":[OSD([sQuery(id+"F0.wireOp",EDGE,"E6.MirrorC")])],"isStart":false});
            fillet(context, id + "F6", {"entities" : qUnion([Q0, Q1, Q2, Q3, Q4, Q5, Q6, Q7, Q8, Q9, Q10, Q11, Q12, Q13, Q14, Q15, Q16, Q17, Q18, Q19, Q20, Q21, Q22, Q23, Q24, Q25, Q26, Q27]), "radius" : .5 * mm, "tangentPropagation" : true, "allowEdgeOverflow" : false});
        }
    });
